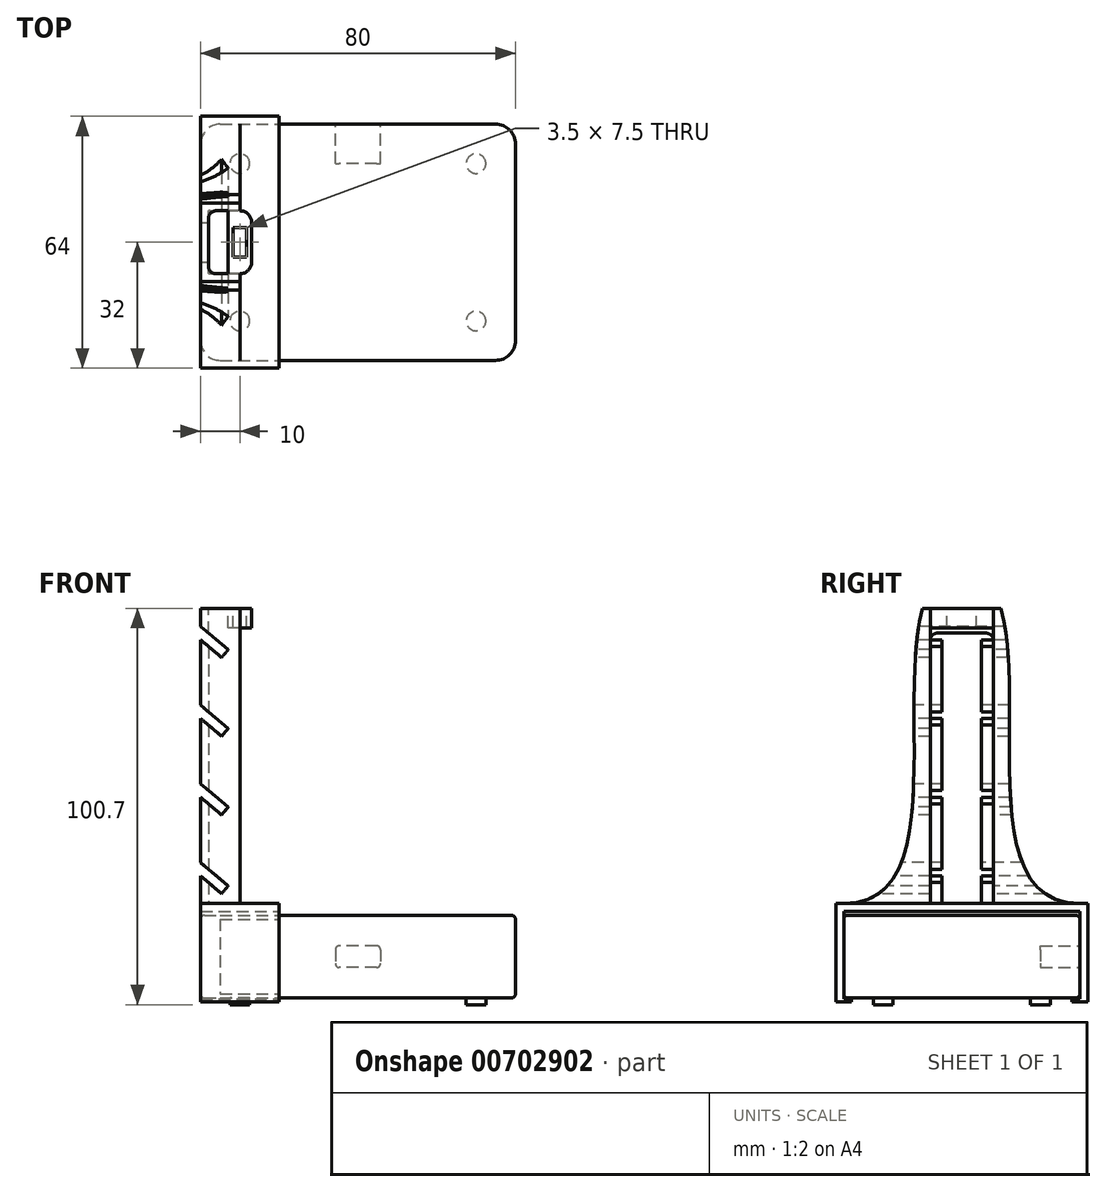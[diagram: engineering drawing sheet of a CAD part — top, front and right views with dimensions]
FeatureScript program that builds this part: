
annotation { "Feature Type Name" : "Feature", "Feature Type Description" : "" }
export const myFeature = defineFeature(function(context is Context, id is Id, definition is map)
    precondition{}
    {
        {
            var Q0;
            Q0=qCreatedBy(makeId("Top.planeOp"),FACE);
            var sketch = newSketch(context, id + "F0", { "sketchPlane" : qUnion([Q0])});
            skLineSegment(sketch, "E0.bottom", {"start": v(0, 0) * mm, "end": v(80, 0) * mm});
            skLineSegment(sketch, "E0.top", {"start": v(0, 60) * mm, "end": v(80, 60) * mm});
            skLineSegment(sketch, "E0.left", {"start": v(0, 0) * mm, "end": v(0, 60) * mm});
            skLineSegment(sketch, "E0.right", {"start": v(80, 0) * mm, "end": v(80, 60) * mm});
            skCircle(sketch, "E1", {"center": v(10, 10) * mm, "radius": 2.5 * mm});
            skCircle(sketch, "E2.0.1.0", {"center": v(10, 50) * mm, "radius": 2.5 * mm});
            skCircle(sketch, "E2.1.0.0", {"center": v(70, 10) * mm, "radius": 2.5 * mm});
            skCircle(sketch, "E2.1.1.0", {"center": v(70, 50) * mm, "radius": 2.5 * mm});
            skLineSegment(sketch, "E2.direction1", {"start": v(10, 10) * mm, "end": v(70, 10) * mm, "construction": true});
            skLineSegment(sketch, "E2.direction2", {"start": v(10, 10) * mm, "end": v(10, 50) * mm, "construction": true});
            skSolve(sketch);
        }
        {
            var Q0;
            Q0=makeQuery(id+"F0.imprint","IMPRINT",FACE,{"disambiguationData":[TD([[makeQuery(id+"F0.imprint","IMPRINT",EDGE,{"derivedFrom":sQuery(id+"F0.wireOp",EDGE,"E0.bottom")}),1.0]])]});
            var Q1;
            Q1=makeQuery(id+"F0.imprint","IMPRINT",FACE,{"disambiguationData":[TD([[makeQuery(id+"F0.imprint","IMPRINT",EDGE,{"derivedFrom":sQuery(id+"F0.wireOp",EDGE,"E1")}),1.0]])]});
            var Q2;
            Q2=makeQuery(id+"F0.imprint","IMPRINT",FACE,{"disambiguationData":[TD([[makeQuery(id+"F0.imprint","IMPRINT",EDGE,{"derivedFrom":sQuery(id+"F0.wireOp",EDGE,"E2.1.0.0")}),1.0]])]});
            var Q3;
            Q3=makeQuery(id+"F0.imprint","IMPRINT",FACE,{"disambiguationData":[TD([[makeQuery(id+"F0.imprint","IMPRINT",EDGE,{"derivedFrom":sQuery(id+"F0.wireOp",EDGE,"E2.1.1.0")}),1.0]])]});
            var Q4;
            Q4=makeQuery(id+"F0.imprint","IMPRINT",FACE,{"disambiguationData":[TD([[makeQuery(id+"F0.imprint","IMPRINT",EDGE,{"derivedFrom":sQuery(id+"F0.wireOp",EDGE,"E2.0.1.0")}),1.0]])]});
            extrude(context, id + "F1", {"entities" : qUnion([Q0, Q1, Q2, Q3, Q4]), "depth" : 21 * mm, "offsetDistance" : 25 * mm});
        }
        {
            var Q0;
            Q0=makeQuery(id+"F1.opExtrude","SWEPT_EDGE",EDGE,{"disambiguationData":[OSD([sQuery(id+"F0.wireOp",EDGE,"E0.bottom"),sQuery(id+"F0.wireOp",EDGE,"E0.left")])]});
            var Q1;
            Q1=makeQuery(id+"F1.opExtrude","SWEPT_EDGE",EDGE,{"disambiguationData":[OSD([sQuery(id+"F0.wireOp",EDGE,"E0.bottom"),sQuery(id+"F0.wireOp",EDGE,"E0.right")])]});
            var Q2;
            Q2=makeQuery(id+"F1.opExtrude","SWEPT_EDGE",EDGE,{"disambiguationData":[OSD([sQuery(id+"F0.wireOp",EDGE,"E0.top"),sQuery(id+"F0.wireOp",EDGE,"E0.right")])]});
            var Q3;
            Q3=makeQuery(id+"F1.opExtrude","SWEPT_EDGE",EDGE,{"disambiguationData":[OSD([sQuery(id+"F0.wireOp",EDGE,"E0.top"),sQuery(id+"F0.wireOp",EDGE,"E0.left")])]});
            fillet(context, id + "F2", {"entities" : qUnion([Q0, Q1, Q2, Q3]), "radius" : 5 * mm, "tangentPropagation" : true, "allowEdgeOverflow" : false});
        }
        {
            var Q0;
            Q0=makeQuery(id+"F1.opExtrude","CAP_EDGE",EDGE,{"disambiguationData":[OSD([sQuery(id+"F0.wireOp",EDGE,"E0.bottom")])],"isStart":false});
            var Q1;
            Q1=makeQuery(id+"F1.opExtrude","CAP_EDGE",EDGE,{"disambiguationData":[OSD([sQuery(id+"F0.wireOp",EDGE,"E0.bottom")])],"isStart":true});
            fillet(context, id + "F3", {"entities" : qUnion([Q0, Q1]), "radius" : 1 * mm, "tangentPropagation" : true, "allowEdgeOverflow" : false});
        }
        {
            var Q0;
            Q0=makeQuery(id+"F1.opExtrude","SWEPT_FACE",FACE,{"disambiguationData":[OSD([sQuery(id+"F0.wireOp",EDGE,"E0.top")])]});
            var sketch = newSketch(context, id + "F4", { "sketchPlane" : qUnion([Q0])});
            skLineSegment(sketch, "E3.0.0", {"start": v(-5, 1) * mm, "end": v(-5, 20) * mm});
            skLineSegment(sketch, "E3.0.1", {"start": v(-5, 20) * mm, "end": v(-75, 20) * mm});
            skLineSegment(sketch, "E3.0.2", {"start": v(-75, 20) * mm, "end": v(-75, 1) * mm});
            skLineSegment(sketch, "E3.0.3", {"start": v(-75, 1) * mm, "end": v(-5, 1) * mm});
            skPoint(sketch, "E4", {"position": v(-40, 20) * mm});
            skPoint(sketch, "E5", {"position": v(-40, 1) * mm});
            skPoint(sketch, "E6", {"position": v(-5, 10.5) * mm});
            skPoint(sketch, "E7", {"position": v(-75, 10.5) * mm});
            skLineSegment(sketch, "E8", {"start": v(-75, 10.5) * mm, "end": v(-5, 10.5) * mm, "construction": true});
            skLineSegment(sketch, "E9", {"start": v(-40, 20) * mm, "end": v(-40, 1) * mm, "construction": true});
            skPoint(sketch, "E10", {"position": v(-40, 10.5) * mm});
            skLineSegment(sketch, "E11.bottom", {"start": v(-44.75, 13.25) * mm, "end": v(-35.25, 13.25) * mm});
            skLineSegment(sketch, "E11.top", {"start": v(-44.75, 7.75) * mm, "end": v(-35.25, 7.75) * mm});
            skLineSegment(sketch, "E11.left", {"start": v(-45.75, 12.25) * mm, "end": v(-45.75, 8.75) * mm});
            skLineSegment(sketch, "E11.right", {"start": v(-34.25, 12.25) * mm, "end": v(-34.25, 8.75) * mm});
            skPoint(sketch, "E12.visualSharp", {"position": v(-45.75, 13.25) * mm});
            skArc(sketch, "E12.filletArc", {"start": v(-44.75, 13.25) * mm, "mid": v(-45.46, 12.96) * mm, "end": v(-45.75, 12.25) * mm});
            skPoint(sketch, "E13.visualSharp", {"position": v(-34.25, 13.25) * mm});
            skArc(sketch, "E13.filletArc", {"start": v(-34.25, 12.25) * mm, "mid": v(-34.54, 12.96) * mm, "end": v(-35.25, 13.25) * mm});
            skPoint(sketch, "E14.visualSharp", {"position": v(-34.25, 7.75) * mm});
            skArc(sketch, "E14.filletArc", {"start": v(-35.25, 7.75) * mm, "mid": v(-34.54, 8.04) * mm, "end": v(-34.25, 8.75) * mm});
            skPoint(sketch, "E15.visualSharp", {"position": v(-45.75, 7.75) * mm});
            skArc(sketch, "E15.filletArc", {"start": v(-45.75, 8.75) * mm, "mid": v(-45.46, 8.04) * mm, "end": v(-44.75, 7.75) * mm});
            skSolve(sketch);
        }
        {
            var Q0;
            Q0=makeQuery(id+"F4.imprint","IMPRINT",FACE,{"disambiguationData":[TD([[makeQuery(id+"F4.imprint","IMPRINT",EDGE,{"derivedFrom":sQuery(id+"F4.wireOp",EDGE,"E11.bottom")}),-1.0]])]});
            extrude(context, id + "F5", {"entities" : qUnion([Q0]), "operationType" : NewBodyOperationType.REMOVE, "oppositeDirection" : true, "depth" : 10 * mm, "offsetDistance" : 25 * mm});
        }
        {
            var Q0;
            Q0=makeQuery(id+"F0.imprint","IMPRINT",FACE,{"disambiguationData":[TD([[makeQuery(id+"F0.imprint","IMPRINT",EDGE,{"derivedFrom":sQuery(id+"F0.wireOp",EDGE,"E1")}),1.0]])]});
            var Q1;
            Q1=makeQuery(id+"F0.imprint","IMPRINT",FACE,{"disambiguationData":[TD([[makeQuery(id+"F0.imprint","IMPRINT",EDGE,{"derivedFrom":sQuery(id+"F0.wireOp",EDGE,"E2.1.0.0")}),1.0]])]});
            var Q2;
            Q2=makeQuery(id+"F0.imprint","IMPRINT",FACE,{"disambiguationData":[TD([[makeQuery(id+"F0.imprint","IMPRINT",EDGE,{"derivedFrom":sQuery(id+"F0.wireOp",EDGE,"E2.1.1.0")}),1.0]])]});
            var Q3;
            Q3=makeQuery(id+"F0.imprint","IMPRINT",FACE,{"disambiguationData":[TD([[makeQuery(id+"F0.imprint","IMPRINT",EDGE,{"derivedFrom":sQuery(id+"F0.wireOp",EDGE,"E2.0.1.0")}),1.0]])]});
            extrude(context, id + "F6", {"entities" : qUnion([Q0, Q1, Q2, Q3]), "operationType" : NewBodyOperationType.ADD, "oppositeDirection" : true, "depth" : 1.7 * mm, "offsetDistance" : 25 * mm});
        }
        {
            var Q0;
            Q0=qCreatedBy(makeId("Front.planeOp"),FACE);
            var sketch = newSketch(context, id + "F7", { "sketchPlane" : qUnion([Q0])});
            skLineSegment(sketch, "E16.0", {"start": v(5, 21) * mm, "end": v(75, 21) * mm, "construction": true});
            skLineSegment(sketch, "E17.0", {"start": v(75, 0) * mm, "end": v(5, 0) * mm, "construction": true});
            skLineSegment(sketch, "E18.bottom", {"start": v(0, -1) * mm, "end": v(20, -1) * mm});
            skLineSegment(sketch, "E18.top", {"start": v(0, 99) * mm, "end": v(20, 99) * mm});
            skLineSegment(sketch, "E18.left", {"start": v(0, -1) * mm, "end": v(0, 99) * mm});
            skLineSegment(sketch, "E18.right", {"start": v(20, -1) * mm, "end": v(20, 99) * mm});
            skLineSegment(sketch, "E19", {"start": v(0, 31) * mm, "end": v(5.36, 26.5) * mm});
            skLineSegment(sketch, "E20", {"start": v(5.36, 26.5) * mm, "end": v(7.03, 28.5) * mm});
            skLineSegment(sketch, "E21", {"start": v(7.03, 28.5) * mm, "end": v(0, 34.4) * mm});
            skLineSegment(sketch, "E22.0.1.0", {"start": v(0, 51) * mm, "end": v(5.36, 46.5) * mm});
            skLineSegment(sketch, "E22.0.1.1", {"start": v(5.36, 46.5) * mm, "end": v(7.03, 48.5) * mm});
            skLineSegment(sketch, "E22.0.1.2", {"start": v(7.03, 48.5) * mm, "end": v(0, 54.4) * mm});
            skLineSegment(sketch, "E22.0.2.0", {"start": v(0, 71) * mm, "end": v(5.36, 66.5) * mm});
            skLineSegment(sketch, "E22.0.2.1", {"start": v(5.36, 66.5) * mm, "end": v(7.03, 68.5) * mm});
            skLineSegment(sketch, "E22.0.2.2", {"start": v(7.03, 68.5) * mm, "end": v(0, 74.4) * mm});
            skLineSegment(sketch, "E22.0.3.0", {"start": v(0, 91) * mm, "end": v(5.36, 86.5) * mm});
            skLineSegment(sketch, "E22.0.3.1", {"start": v(5.36, 86.5) * mm, "end": v(7.03, 88.5) * mm});
            skLineSegment(sketch, "E22.0.3.2", {"start": v(7.03, 88.5) * mm, "end": v(0, 94.4) * mm});
            skLineSegment(sketch, "E22.direction1", {"start": v(0, 31) * mm, "end": v(25, 31) * mm, "construction": true});
            skLineSegment(sketch, "E22.direction2", {"start": v(0, 31) * mm, "end": v(0, 51) * mm, "construction": true});
            skLineSegment(sketch, "E23", {"start": v(10, 99) * mm, "end": v(10, 24) * mm});
            skLineSegment(sketch, "E24", {"start": v(0, 24) * mm, "end": v(20, 24) * mm});
            skLineSegment(sketch, "E25", {"start": v(0, 22) * mm, "end": v(20, 22) * mm});
            skLineSegment(sketch, "E26", {"start": v(0, -0.2) * mm, "end": v(20, -0.2) * mm});
            skSolve(sketch);
        }
        {
            var Q0;
            {var subQ0=sQuery(id+"F7.wireOp",EDGE,"E18.bottom");Q0=makeQuery(id+"F7.imprint","IMPRINT",FACE,{"disambiguationData":[TD([[makeQuery(id+"F7.imprint","IMPRINT",EDGE,{"derivedFrom":subQ0}),1.0]])]});}
            var Q1;
            {var subQ6=sQuery(id+"F7.wireOp",EDGE,"E25");Q1=makeQuery(id+"F7.imprint","IMPRINT",FACE,{"disambiguationData":[TD([[makeQuery(id+"F7.imprint","IMPRINT",EDGE,{"derivedFrom":subQ6}),1.0]])]});}
            var Q2;
            {var subQ0=sQuery(id+"F7.wireOp",EDGE,"E25");Q2=makeQuery(id+"F7.imprint","IMPRINT",FACE,{"disambiguationData":[TD([[makeQuery(id+"F7.imprint","IMPRINT",EDGE,{"derivedFrom":subQ0}),-1.0]])]});}
            extrude(context, id + "F8", {"entities" : qUnion([Q0, Q1, Q2]), "depth" : 2 * mm, "offsetDistance" : 25 * mm});
        }
        {
            var Q0;
            {var subQ6=sQuery(id+"F7.wireOp",EDGE,"E25");Q0=makeQuery(id+"F7.imprint","IMPRINT",FACE,{"disambiguationData":[TD([[makeQuery(id+"F7.imprint","IMPRINT",EDGE,{"derivedFrom":subQ6}),1.0]])]});}
            var Q1;
            {var subQ1=sQuery(id+"F7.wireOp",EDGE,"E19");Q1=makeQuery(id+"F7.imprint","IMPRINT",FACE,{"disambiguationData":[TD([[makeQuery(id+"F7.imprint","IMPRINT",EDGE,{"derivedFrom":subQ1}),-1.0]])]});}
            var Q2;
            Q2=makeQuery(id+"F1.opExtrude","SWEPT_FACE",FACE,{"disambiguationData":[OSD([sQuery(id+"F0.wireOp",EDGE,"E0.top")])]});
            extrude(context, id + "F9", {"entities" : qUnion([Q0, Q1]), "operationType" : NewBodyOperationType.ADD, "endBound" : BoundingType.UP_TO_SURFACE, "oppositeDirection" : true, "depth" : 58.3 * mm, "endBoundEntityFace" : qUnion([Q2]), "offsetDistance" : 25 * mm});
        }
        {
            var Q0;
            Q0=makeQuery(id+"F9.opExtrude","CAP_FACE",FACE,{"disambiguationData":[OSD([sQuery(id+"F7.wireOp",EDGE,"E18.top"),sQuery(id+"F7.wireOp",EDGE,"E18.left"),sQuery(id+"F7.wireOp",EDGE,"E18.right"),sQuery(id+"F7.wireOp",EDGE,"E19"),sQuery(id+"F7.wireOp",EDGE,"E20"),sQuery(id+"F7.wireOp",EDGE,"E21"),sQuery(id+"F7.wireOp",EDGE,"E22.0.1.0"),sQuery(id+"F7.wireOp",EDGE,"E22.0.1.1"),sQuery(id+"F7.wireOp",EDGE,"E22.0.1.2"),sQuery(id+"F7.wireOp",EDGE,"E22.0.2.0"),sQuery(id+"F7.wireOp",EDGE,"E22.0.2.1"),sQuery(id+"F7.wireOp",EDGE,"E22.0.2.2"),sQuery(id+"F7.wireOp",EDGE,"E22.0.3.0"),sQuery(id+"F7.wireOp",EDGE,"E22.0.3.1"),sQuery(id+"F7.wireOp",EDGE,"E22.0.3.2"),sQuery(id+"F7.wireOp",EDGE,"E23"),sQuery(id+"F7.wireOp",EDGE,"E24"),sQuery(id+"F7.wireOp",EDGE,"E25")])],"isStart":false});
            var sketch = newSketch(context, id + "F10", { "sketchPlane" : qUnion([Q0])});
            skLineSegment(sketch, "E27.0.1", {"start": v(0, 22) * mm, "end": v(0, -1) * mm});
            skLineSegment(sketch, "E27.0.3", {"start": v(-20, -1) * mm, "end": v(-20, 22) * mm});
            skLineSegment(sketch, "E28.0", {"start": v(0, 24) * mm, "end": v(-20, 24) * mm});
            skLineSegment(sketch, "E29", {"start": v(-20, 24) * mm, "end": v(-20, 22) * mm});
            skLineSegment(sketch, "E30", {"start": v(0, 24) * mm, "end": v(0, 22) * mm});
            skLineSegment(sketch, "E31.0", {"start": v(0, -0.2) * mm, "end": v(-20, -0.2) * mm});
            skLineSegment(sketch, "E32.0", {"start": v(0, 22) * mm, "end": v(-20, 22) * mm});
            skLineSegment(sketch, "E33.0", {"start": v(0, -1) * mm, "end": v(-20, -1) * mm});
            skSolve(sketch);
        }
        {
            var Q0;
            Q0 = qSketchRegion(id + "F10", true);
            extrude(context, id + "F11", {"entities" : qUnion([Q0]), "operationType" : NewBodyOperationType.ADD, "depth" : 2 * mm, "offsetDistance" : 25 * mm});
        }
        {
            var Q0;
            Q0=makeQuery(id+"F9.opExtrude","SWEPT_FACE",FACE,{"disambiguationData":[OSD([sQuery(id+"F7.wireOp",EDGE,"E23")])]});
            var sketch = newSketch(context, id + "F12", { "sketchPlane" : qUnion([Q0])});
            skLineSegment(sketch, "E34.0.0", {"start": v(60, 24) * mm, "end": v(60, 99) * mm});
            skLineSegment(sketch, "E34.0.1", {"start": v(60, 99) * mm, "end": v(0, 99) * mm});
            skLineSegment(sketch, "E34.0.2", {"start": v(0, 99) * mm, "end": v(0, 24) * mm});
            skLineSegment(sketch, "E34.0.3", {"start": v(0, 24) * mm, "end": v(60, 24) * mm});
            skLineSegment(sketch, "E35", {"start": v(20, 99) * mm, "end": v(40, 99) * mm});
            skPoint(sketch, "E36", {"position": v(30, 99) * mm});
            skFitSpline(sketch, "E37", {"points": [v(20, 99) * mm, v(0, 24) * mm], "startDerivative": vector(-20, -75) * mm, "endDerivative": vector(-81.59, 0) * mm});
            skLineSegment(sketch, "E38", {"start": v(20, 99) * mm, "end": v(20, 24) * mm, "construction": true});
            skLineSegment(sketch, "E39", {"start": v(40, 99) * mm, "end": v(40, 24) * mm, "construction": true});
            skLineSegment(sketch, "E40", {"start": v(30, 99) * mm, "end": v(30, 24) * mm, "construction": true});
            skFitSpline(sketch, "E41.MirrorCS", {"points": [v(40, 99) * mm, v(60, 24) * mm], "startDerivative": vector(20, -75) * mm, "endDerivative": vector(81.59, 0) * mm});
            skSolve(sketch);
        }
        {
            var Q0;
            {var subQ0=sQuery(id+"F12.wireOp",EDGE,"E34.0.2");Q0=makeQuery(id+"F12.imprint","IMPRINT",FACE,{"disambiguationData":[TD([[makeQuery(id+"F12.imprint","IMPRINT",EDGE,{"derivedFrom":subQ0}),1.0]])]});}
            var Q1;
            {var subQ0=sQuery(id+"F12.wireOp",EDGE,"E34.0.0");Q1=makeQuery(id+"F12.imprint","IMPRINT",FACE,{"disambiguationData":[TD([[makeQuery(id+"F12.imprint","IMPRINT",EDGE,{"derivedFrom":subQ0}),-1.0]])]});}
            extrude(context, id + "F13", {"entities" : qUnion([Q0, Q1]), "operationType" : NewBodyOperationType.REMOVE, "oppositeDirection" : true, "depth" : 25 * mm, "offsetDistance" : 25 * mm});
        }
        {
            var Q0;
            Q0=makeQuery(id+"F9.opExtrude","SWEPT_FACE",FACE,{"disambiguationData":[OSD([sQuery(id+"F7.wireOp",EDGE,"E18.top")])]});
            var sketch = newSketch(context, id + "F14", { "sketchPlane" : qUnion([Q0])});
            skLineSegment(sketch, "E42.0.0", {"start": v(0, 40) * mm, "end": v(0, 20) * mm});
            skLineSegment(sketch, "E42.0.1", {"start": v(0, 20) * mm, "end": v(10, 20) * mm});
            skLineSegment(sketch, "E42.0.2", {"start": v(10, 20) * mm, "end": v(10, 40) * mm});
            skLineSegment(sketch, "E42.0.3", {"start": v(10, 40) * mm, "end": v(0, 40) * mm});
            skLineSegment(sketch, "E43.bottom", {"start": v(10, 38) * mm, "end": v(2, 38) * mm});
            skLineSegment(sketch, "E43.top", {"start": v(10, 22) * mm, "end": v(2, 22) * mm});
            skLineSegment(sketch, "E43.left", {"start": v(10, 38) * mm, "end": v(10, 22) * mm});
            skLineSegment(sketch, "E43.right", {"start": v(2, 38) * mm, "end": v(2, 22) * mm});
            skSolve(sketch);
        }
        {
            var Q0;
            Q0=makeQuery(id+"F14.imprint","IMPRINT",FACE,{"disambiguationData":[TD([[makeQuery(id+"F14.imprint","IMPRINT",EDGE,{"derivedFrom":sQuery(id+"F14.wireOp",EDGE,"E43.bottom")}),1.0]])]});
            var Q1;
            {var subQ0=sQuery(id+"F7.wireOp",EDGE,"E24");Q1=makeQuery(id+"F11.boolean.opBoolean","MERGE",FACE,{"derivedFrom":[makeQuery(id+"F9.boolean.opBoolean","MERGE",FACE,{"derivedFrom":[makeQuery(id+"F8.opExtrude","SWEPT_FACE",FACE,{"disambiguationData":[OSD([subQ0])]}),makeQuery(id+"F9.opExtrude","SWEPT_FACE",FACE,{"disambiguationData":[OSD([subQ0])]})]}),makeQuery(id+"F11.opExtrude","SWEPT_FACE",FACE,{"disambiguationData":[OSD([sQuery(id+"F10.wireOp",EDGE,"E28.0")])]})]});}
            extrude(context, id + "F15", {"entities" : qUnion([Q0]), "operationType" : NewBodyOperationType.REMOVE, "endBound" : BoundingType.UP_TO_SURFACE, "oppositeDirection" : true, "depth" : 25 * mm, "endBoundEntityFace" : qUnion([Q1]), "offsetDistance" : 25 * mm});
        }
        {
            var Q0;
            Q0=makeQuery(id+"F15.boolean.opBoolean","SPLIT",FACE,{"disambiguationData":[TD([makeQuery(id+"F13.boolean.opBoolean","COPY",FACE,{"derivedFrom":makeQuery(id+"F13.opExtrude","SWEPT_FACE",FACE,{"disambiguationData":[OSD([sQuery(id+"F12.wireOp",EDGE,"E41.MirrorCS")])]})})])],"derivedFrom":makeQuery(id+"F9.opExtrude","SWEPT_FACE",FACE,{"disambiguationData":[OSD([sQuery(id+"F7.wireOp",EDGE,"E23")])]})});
            var sketch = newSketch(context, id + "F16", { "sketchPlane" : qUnion([Q0])});
            skLineSegment(sketch, "E44.0", {"start": v(22, 24) * mm, "end": v(22, 99) * mm});
            skLineSegment(sketch, "E45.0", {"start": v(38, 24) * mm, "end": v(38, 99) * mm});
            skLineSegment(sketch, "E46", {"start": v(22, 99) * mm, "end": v(38, 99) * mm});
            skLineSegment(sketch, "E47", {"start": v(22, 94) * mm, "end": v(38, 94) * mm});
            skSolve(sketch);
        }
        {
            var Q0;
            Q0 = qSketchRegion(id + "F16", true);
            extrude(context, id + "F17", {"entities" : qUnion([Q0]), "operationType" : NewBodyOperationType.ADD, "endBound" : BoundingType.SYMMETRIC, "depth" : 6 * mm, "offsetDistance" : 25 * mm});
        }
        {
            var Q0;
            Q0=makeQuery(id+"F17.opExtrude","CAP_EDGE",EDGE,{"disambiguationData":[OSD([sQuery(id+"F16.wireOp",EDGE,"E44.0")])],"isStart":false});
            var Q1;
            Q1=makeQuery(id+"F17.opExtrude","CAP_EDGE",EDGE,{"disambiguationData":[OSD([sQuery(id+"F16.wireOp",EDGE,"E45.0")])],"isStart":false});
            fillet(context, id + "F18", {"entities" : qUnion([Q0, Q1]), "radius" : 3 * mm, "tangentPropagation" : true, "allowEdgeOverflow" : false});
        }
        {
            var Q0;
            Q0=makeQuery(id+"F17.boolean.opBoolean","MERGE",FACE,{"derivedFrom":[makeQuery(id+"F9.opExtrude","SWEPT_FACE",FACE,{"disambiguationData":[OSD([sQuery(id+"F7.wireOp",EDGE,"E18.top")])]}),makeQuery(id+"F17.opExtrude","SWEPT_FACE",FACE,{"disambiguationData":[OSD([sQuery(id+"F16.wireOp",EDGE,"E46")])]})]});
            var sketch = newSketch(context, id + "F19", { "sketchPlane" : qUnion([Q0])});
            skLineSegment(sketch, "E48.0.0", {"start": v(13, 25) * mm, "end": v(13, 35) * mm});
            skArc(sketch, "E48.0.1", {"start": v(13, 35) * mm, "mid": v(12.12, 37.12) * mm, "end": v(10, 38) * mm});
            skLineSegment(sketch, "E48.0.2", {"start": v(10, 38) * mm, "end": v(10, 40) * mm});
            skLineSegment(sketch, "E48.0.3", {"start": v(10, 40) * mm, "end": v(0, 40) * mm});
            skLineSegment(sketch, "E48.0.4", {"start": v(0, 40) * mm, "end": v(0, 20) * mm});
            skLineSegment(sketch, "E48.0.5", {"start": v(0, 20) * mm, "end": v(10, 20) * mm});
            skLineSegment(sketch, "E48.0.6", {"start": v(10, 20) * mm, "end": v(10, 22) * mm});
            skArc(sketch, "E48.0.7", {"start": v(10, 22) * mm, "mid": v(12.12, 22.88) * mm, "end": v(13, 25) * mm});
            skPoint(sketch, "E49", {"position": v(7, 30) * mm});
            skPoint(sketch, "E50", {"position": v(13, 30) * mm});
            skLineSegment(sketch, "E51", {"start": v(7, 30) * mm, "end": v(13, 30) * mm, "construction": true});
            skPoint(sketch, "E52", {"position": v(10, 30) * mm});
            skLineSegment(sketch, "E53", {"start": v(10, 22) * mm, "end": v(10, 38) * mm, "construction": true});
            skLineSegment(sketch, "E54.bottom", {"start": v(8.25, 26.25) * mm, "end": v(11.75, 26.25) * mm});
            skLineSegment(sketch, "E54.top", {"start": v(8.25, 33.75) * mm, "end": v(11.75, 33.75) * mm});
            skLineSegment(sketch, "E54.left", {"start": v(8.25, 26.25) * mm, "end": v(8.25, 33.75) * mm});
            skLineSegment(sketch, "E54.right", {"start": v(11.75, 26.25) * mm, "end": v(11.75, 33.75) * mm});
            skSolve(sketch);
        }
        {
            var Q0;
            Q0=makeQuery(id+"F19.imprint","IMPRINT",FACE,{"disambiguationData":[TD([[makeQuery(id+"F19.imprint","IMPRINT",EDGE,{"derivedFrom":sQuery(id+"F19.wireOp",EDGE,"E54.bottom")}),1.0]])]});
            var Q1;
            Q1=makeQuery(id+"F17.opExtrude","SWEPT_FACE",FACE,{"disambiguationData":[OSD([sQuery(id+"F16.wireOp",EDGE,"E47")])]});
            extrude(context, id + "F20", {"entities" : qUnion([Q0]), "operationType" : NewBodyOperationType.REMOVE, "endBound" : BoundingType.UP_TO_SURFACE, "oppositeDirection" : true, "depth" : 7.2 * mm, "endBoundEntityFace" : qUnion([Q1]), "offsetDistance" : 25 * mm});
        }
        {
            var Q0;
            {var subQ0=sQuery(id+"F7.wireOp",EDGE,"E18.left");Q0=makeQuery(id+"F9.opExtrude","SWEPT_FACE",FACE,{"disambiguationData":[OSD([subQ0]),TDD([makeQuery(id+"F7.imprint","IMPRINT",EDGE,{"disambiguationData":[TD([[makeQuery(id+"F7.imprint","INTERSECT",VERTEX,{"derivedFrom":[subQ0,sQuery(id+"F7.wireOp",EDGE,"E22.0.2.2")]}),-1.0]])],"derivedFrom":subQ0})])]});}
            var sketch = newSketch(context, id + "F21", { "sketchPlane" : qUnion([Q0])});
            skLineSegment(sketch, "E55.0", {"start": v(-41.43, 91) * mm, "end": v(-18.57, 91) * mm});
            skLineSegment(sketch, "E56.0", {"start": v(2, 24) * mm, "end": v(-62, 24) * mm});
            skPoint(sketch, "E57", {"position": v(-30, 91) * mm});
            skPoint(sketch, "E58", {"position": v(-30, 24) * mm});
            skLineSegment(sketch, "E59", {"start": v(-30, 91) * mm, "end": v(-30, 24) * mm, "construction": true});
            skLineSegment(sketch, "E60", {"start": v(-35, 91) * mm, "end": v(-25, 91) * mm});
            skLineSegment(sketch, "E61", {"start": v(-35, 91) * mm, "end": v(-35, 24) * mm});
            skLineSegment(sketch, "E62", {"start": v(-25, 91) * mm, "end": v(-25, 24) * mm});
            skSolve(sketch);
        }
        {
            var Q0;
            Q0 = qSketchRegion(id + "F21", true);
            extrude(context, id + "F22", {"entities" : qUnion([Q0]), "operationType" : NewBodyOperationType.REMOVE, "oppositeDirection" : true, "depth" : 25 * mm, "offsetDistance" : 25 * mm});
        }
        {
            var Q0;
            {var subQ0=sQuery(id+"F7.wireOp",EDGE,"E18.bottom");Q0=makeQuery(id+"F7.imprint","IMPRINT",FACE,{"disambiguationData":[TD([[makeQuery(id+"F7.imprint","IMPRINT",EDGE,{"derivedFrom":subQ0}),1.0]])]});}
            extrude(context, id + "F23", {"entities" : qUnion([Q0]), "operationType" : NewBodyOperationType.ADD, "oppositeDirection" : true, "depth" : 2 * mm, "offsetDistance" : 25 * mm});
        }
        {
            var Q0;
            {var subQ2=sQuery(id+"F10.wireOp",EDGE,"E31.0");Q0=makeQuery(id+"F10.imprint","IMPRINT",FACE,{"disambiguationData":[TD([[makeQuery(id+"F10.imprint","IMPRINT",EDGE,{"derivedFrom":subQ2}),1.0]])]});}
            extrude(context, id + "F24", {"entities" : qUnion([Q0]), "operationType" : NewBodyOperationType.ADD, "oppositeDirection" : true, "depth" : 2 * mm, "offsetDistance" : 25 * mm});
        }
        {
            var Q0;
            Q0=makeQuery(id+"F17.opExtrude","CAP_EDGE",EDGE,{"disambiguationData":[OSD([sQuery(id+"F16.wireOp",EDGE,"E45.0")])],"isStart":true});
            var Q1;
            {var subQ0=sQuery(id+"F14.wireOp",EDGE,"E43.bottom");var subQ1=sQuery(id+"F14.wireOp",EDGE,"E43.right");Q1=makeQuery(id+"F15.boolean.opBoolean","COPY",EDGE,{"disambiguationData":[TD([makeQuery(id+"F9.opExtrude","SWEPT_FACE",FACE,{"disambiguationData":[OSD([sQuery(id+"F7.wireOp",EDGE,"E18.top")])]})])],"derivedFrom":makeQuery(id+"F15.opExtrude","SWEPT_EDGE",EDGE,{"disambiguationData":[OSD([subQ0,subQ1])]})});}
            var Q2;
            {var subQ0=sQuery(id+"F14.wireOp",EDGE,"E43.top");var subQ1=sQuery(id+"F14.wireOp",EDGE,"E43.right");Q2=makeQuery(id+"F15.boolean.opBoolean","COPY",EDGE,{"disambiguationData":[TD([makeQuery(id+"F9.opExtrude","SWEPT_FACE",FACE,{"disambiguationData":[OSD([sQuery(id+"F7.wireOp",EDGE,"E18.top")])]})])],"derivedFrom":makeQuery(id+"F15.opExtrude","SWEPT_EDGE",EDGE,{"disambiguationData":[OSD([subQ0,subQ1])]})});}
            var Q3;
            Q3=makeQuery(id+"F17.opExtrude","CAP_EDGE",EDGE,{"disambiguationData":[OSD([sQuery(id+"F16.wireOp",EDGE,"E44.0")])],"isStart":true});
            fillet(context, id + "F25", {"entities" : qUnion([Q0, Q1, Q2, Q3]), "radius" : 2 * mm, "tangentPropagation" : true, "allowEdgeOverflow" : false});
        }
    });
